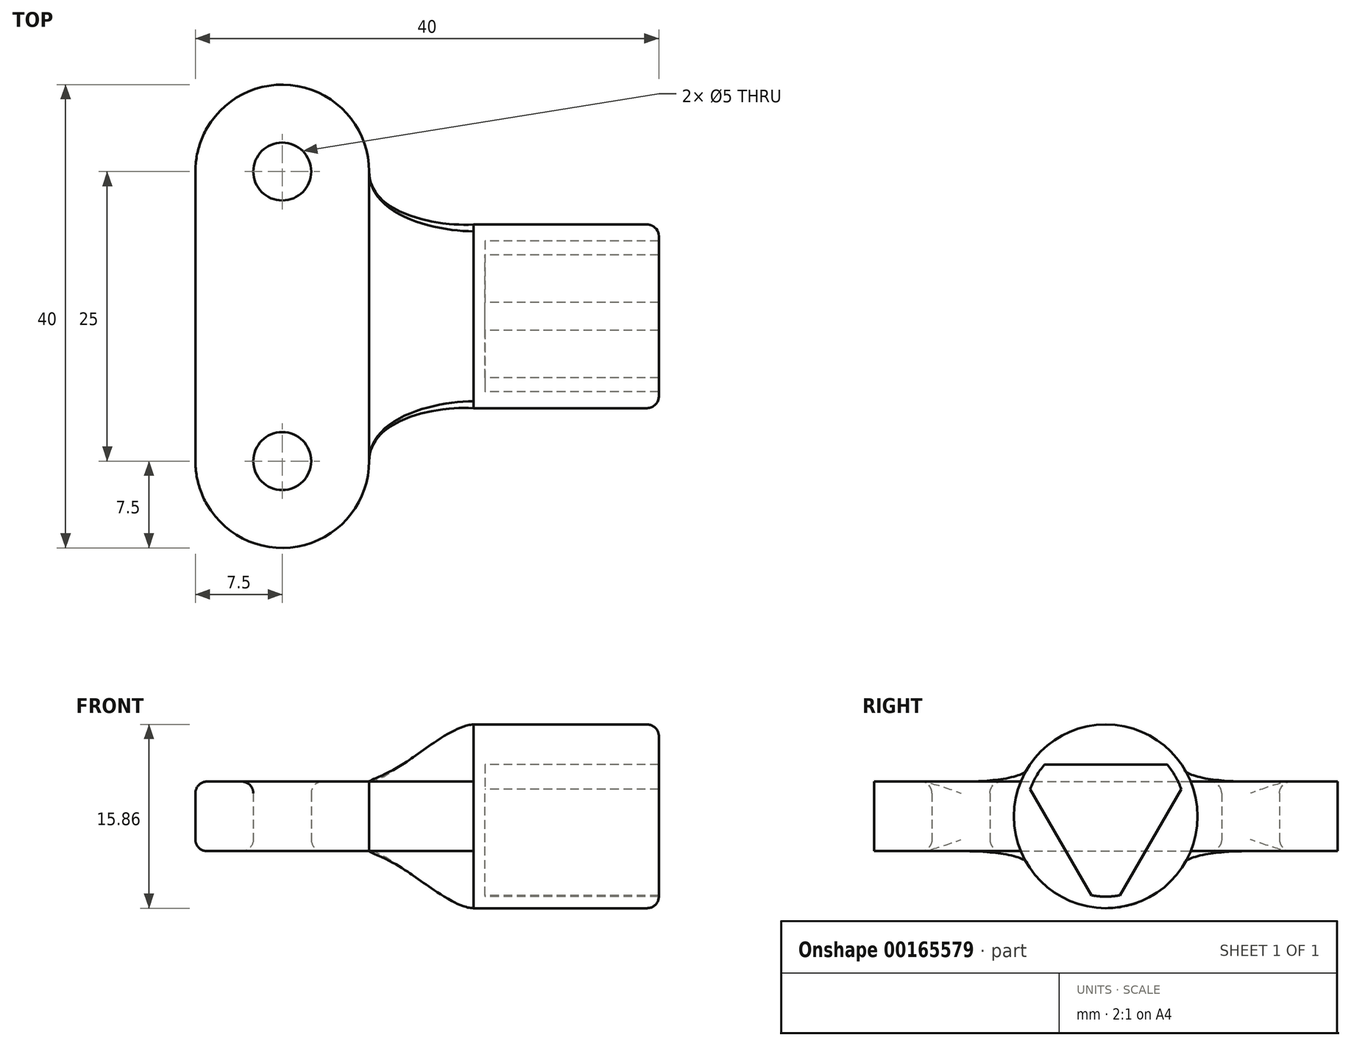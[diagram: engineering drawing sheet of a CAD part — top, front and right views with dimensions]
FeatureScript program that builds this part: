
annotation { "Feature Type Name" : "Feature", "Feature Type Description" : "" }
export const myFeature = defineFeature(function(context is Context, id is Id, definition is map)
    precondition{}
    {
        {
            var Q0;
            Q0=qCreatedBy(makeId("Right.planeOp"),FACE);
            cPlane(context, id + "F0", {"entities" : qUnion([Q0]), "cplaneType" : CPlaneType.OFFSET, "offset" : 0 * mm, "width" : 152.4 * mm, "height" : 152.4 * mm});
        }
        {
            var Q0;
            Q0=qCreatedBy(id+"F0.planeOp",FACE);
            var sketch = newSketch(context, id + "F1", { "sketchPlane" : qUnion([Q0])});
            skCircle(sketch, "E0", {"center": v(0, 0) * mm, "radius": 7.93 * mm});
            skCircle(sketch, "E1", {"center": v(0, 0) * mm, "radius": 6.93 * mm});
            skLineSegment(sketch, "E2", {"start": v(-5.3, 4.46) * mm, "end": v(5.3, 4.46) * mm});
            skLineSegment(sketch, "E3.1.0", {"start": v(-1.22, -6.82) * mm, "end": v(-6.52, 2.36) * mm});
            skLineSegment(sketch, "E3.2.0", {"start": v(6.52, 2.36) * mm, "end": v(1.22, -6.82) * mm});
            skCircle(sketch, "E4.cCircle", {"center": v(0, 0) * mm, "radius": 6.93 * mm, "construction": true});
            skLineSegment(sketch, "E4.0", {"start": v(0, -6.93) * mm, "end": v(-6, 3.46) * mm});
            skLineSegment(sketch, "E4.1", {"start": v(-6, 3.46) * mm, "end": v(6, 3.46) * mm});
            skLineSegment(sketch, "E4.2", {"start": v(6, 3.46) * mm, "end": v(0, -6.93) * mm});
            skLineSegment(sketch, "E5.bottom", {"start": v(-20, -7.93) * mm, "end": v(20, -7.93) * mm});
            skLineSegment(sketch, "E5.top", {"start": v(-20, 7.93) * mm, "end": v(20, 7.93) * mm});
            skLineSegment(sketch, "E5.left", {"start": v(-20, -7.93) * mm, "end": v(-20, 7.93) * mm});
            skLineSegment(sketch, "E5.right", {"start": v(20, -7.93) * mm, "end": v(20, 7.93) * mm});
            skSolve(sketch);
        }
        {
            var Q0;
            Q0=makeQuery(id+"F1.imprint","IMPRINT",FACE,{"disambiguationData":[TD([[makeQuery(id+"F1.imprint","IMPRINT",EDGE,{"derivedFrom":sQuery(id+"F1.wireOp",EDGE,"E0")}),1.0]])]});
            var Q1;
            {var subQ0=sQuery(id+"F1.wireOp",EDGE,"E2");Q1=makeQuery(id+"F1.imprint","IMPRINT",FACE,{"disambiguationData":[TD([[makeQuery(id+"F1.imprint","IMPRINT",EDGE,{"derivedFrom":subQ0}),1.0]])]});}
            var Q2;
            {var subQ0=sQuery(id+"F1.wireOp",EDGE,"E3.1.0");Q2=makeQuery(id+"F1.imprint","IMPRINT",FACE,{"disambiguationData":[TD([[makeQuery(id+"F1.imprint","IMPRINT",EDGE,{"derivedFrom":subQ0}),1.0]])]});}
            var Q3;
            {var subQ0=sQuery(id+"F1.wireOp",EDGE,"E3.2.0");Q3=makeQuery(id+"F1.imprint","IMPRINT",FACE,{"disambiguationData":[TD([[makeQuery(id+"F1.imprint","IMPRINT",EDGE,{"derivedFrom":subQ0}),1.0]])]});}
            var Q4;
            Q4=sQuery(id+"F1.wireOp",EDGE,"E0");
            var Q5;
            Q5=sQuery(id+"F1.wireOp",EDGE,"E1");
            var Q6;
            Q6=sQuery(id+"F1.wireOp",EDGE,"E2");
            var Q7;
            Q7=sQuery(id+"F1.wireOp",EDGE,"E3.1.0");
            var Q8;
            Q8=sQuery(id+"F1.wireOp",EDGE,"E3.2.0");
            extrude(context, id + "F2", {"entities" : qUnion([Q0, Q1, Q2, Q3]), "surfaceEntities" : qUnion([Q4, Q5, Q6, Q7, Q8]), "depth" : 15 * mm});
        }
        {
            var Q0;
            Q0=qCreatedBy(makeId("Top.planeOp"),FACE);
            var sketch = newSketch(context, id + "F3", { "sketchPlane" : qUnion([Q0])});
            skLineSegment(sketch, "E6", {"start": v(0, 0) * mm, "end": v(-7.34, 0) * mm, "construction": true});
            skLineSegment(sketch, "E7", {"start": v(-5, -7.93) * mm, "end": v(-5, -7.93) * mm});
            skLineSegment(sketch, "E8.trimOffspring", {"start": v(-12.53, 0) * mm, "end": v(-38.9, 0) * mm, "construction": true});
            skPoint(sketch, "E9.0.start.orphan", {"position": v(0, 7.93) * mm});
            skCircle(sketch, "E10", {"center": v(-17.5, -12.5) * mm, "radius": 2.5 * mm});
            skArc(sketch, "E11", {"start": v(-25, -12.5) * mm, "mid": v(-17.5, -20) * mm, "end": v(-10, -12.5) * mm});
            skLineSegment(sketch, "E12", {"start": v(-25, -12.5) * mm, "end": v(-25, 0) * mm});
            skLineSegment(sketch, "E13", {"start": v(-10, -12.5) * mm, "end": v(-10, 0) * mm});
            skLineSegment(sketch, "E14.MirrorCS", {"start": v(-10, 12.5) * mm, "end": v(-10, 0) * mm});
            skArc(sketch, "E15.MirrorCS", {"start": v(-25, 12.5) * mm, "mid": v(-17.5, 20) * mm, "end": v(-10, 12.5) * mm});
            skLineSegment(sketch, "E16.MirrorCS", {"start": v(-25, 12.5) * mm, "end": v(-25, 0) * mm});
            skCircle(sketch, "E17.MirrorC", {"center": v(-17.5, 12.5) * mm, "radius": 2.5 * mm});
            skSolve(sketch);
        }
        {
            var Q0;
            Q0=makeQuery(id+"F3.imprint","IMPRINT",FACE,{"disambiguationData":[TD([[makeQuery(id+"F3.imprint","IMPRINT",EDGE,{"derivedFrom":sQuery(id+"F3.wireOp",EDGE,"E10")}),-1.0]])]});
            extrude(context, id + "F4", {"entities" : qUnion([Q0]), "endBound" : BoundingType.SYMMETRIC, "depth" : 6 * mm});
        }
        {
            var Q0;
            Q0=qCreatedBy(makeId("Right.planeOp"),FACE);
            var sketch = newSketch(context, id + "F5", { "sketchPlane" : qUnion([Q0])});
            skArc(sketch, "E18.0", {"start": v(-7.93, 0) * mm, "mid": v(0, -7.93) * mm, "end": v(7.93, 0) * mm});
            skArc(sketch, "E19.0", {"start": v(7.93, 0) * mm, "mid": v(0, 7.93) * mm, "end": v(-7.93, 0) * mm});
            skLineSegment(sketch, "E20.bottom", {"start": v(-35.1, -7.93) * mm, "end": v(32.55, -7.93) * mm});
            skLineSegment(sketch, "E20.top", {"start": v(-35.1, 7.93) * mm, "end": v(32.55, 7.93) * mm});
            skLineSegment(sketch, "E20.left", {"start": v(-35.1, -7.93) * mm, "end": v(-35.1, 7.93) * mm});
            skLineSegment(sketch, "E20.right", {"start": v(32.55, -7.93) * mm, "end": v(32.55, 7.93) * mm});
            skSolve(sketch);
        }
        {
            var Q0;
            Q0=makeQuery(id+"F2.opExtrude","CAP_FACE",FACE,{"disambiguationData":[OSD([sQuery(id+"F1.wireOp",EDGE,"E0"),sQuery(id+"F1.wireOp",EDGE,"E1"),sQuery(id+"F1.wireOp",EDGE,"E2"),sQuery(id+"F1.wireOp",EDGE,"E3.1.0"),sQuery(id+"F1.wireOp",EDGE,"E3.2.0")])],"isStart":true});
            var sketch = newSketch(context, id + "F6", { "sketchPlane" : qUnion([Q0])});
            skCircle(sketch, "E21.0", {"center": v(0, 0) * mm, "radius": 7.93 * mm});
            skSolve(sketch);
        }
        {
            var Q0;
            {var subQ5=sQuery(id+"F1.wireOp",EDGE,"E2");Q0=makeQuery(id+"F6.imprint","IMPRINT",FACE,{"disambiguationData":[TD([[makeQuery(id+"F6.imprint","IMPRINT",EDGE,{"derivedFrom":makeQuery(id+"F2.opExtrude","CAP_EDGE",EDGE,{"disambiguationData":[OSD([subQ5])],"isStart":true})}),1.0]])]});}
            var Q1;
            Q1=makeQuery(id+"F6.imprint","IMPRINT",FACE,{"disambiguationData":[TD([[makeQuery(id+"F6.imprint","IMPRINT",EDGE,{"derivedFrom":sQuery(id+"F6.wireOp",EDGE,"E21.0")}),-1.0]])]});
            extrude(context, id + "F7", {"entities" : qUnion([Q0, Q1]), "operationType" : NewBodyOperationType.ADD, "depth" : 1 * mm});
        }
        {
            var Q0;
            Q0=makeQuery(id+"F4.opExtrude","CAP_FACE",FACE,{"disambiguationData":[OSD([sQuery(id+"F3.wireOp",EDGE,"E10"),sQuery(id+"F3.wireOp",EDGE,"E11"),sQuery(id+"F3.wireOp",EDGE,"E12"),sQuery(id+"F3.wireOp",EDGE,"E13"),sQuery(id+"F3.wireOp",EDGE,"E14.MirrorCS"),sQuery(id+"F3.wireOp",EDGE,"E15.MirrorCS"),sQuery(id+"F3.wireOp",EDGE,"E16.MirrorCS"),sQuery(id+"F3.wireOp",EDGE,"E17.MirrorC")])],"isStart":false});
            var sketch = newSketch(context, id + "F8", { "sketchPlane" : qUnion([Q0])});
            skFitSpline(sketch, "E22", {"points": [v(-1, -7.34) * mm, v(-10, -12.5) * mm], "startDerivative": vector(-9.67, 0) * mm, "endDerivative": vector(0, -11.48) * mm});
            skFitSpline(sketch, "E23.MirrorCS", {"points": [v(-1, 7.34) * mm, v(-10, 12.5) * mm], "startDerivative": vector(-9.67, 0) * mm, "endDerivative": vector(0, 11.48) * mm});
            skSolve(sketch);
        }
        {
            var Q0;
            Q0=makeQuery(id+"F4.opExtrude","CAP_FACE",FACE,{"disambiguationData":[OSD([sQuery(id+"F3.wireOp",EDGE,"E10"),sQuery(id+"F3.wireOp",EDGE,"E11"),sQuery(id+"F3.wireOp",EDGE,"E12"),sQuery(id+"F3.wireOp",EDGE,"E13"),sQuery(id+"F3.wireOp",EDGE,"E14.MirrorCS"),sQuery(id+"F3.wireOp",EDGE,"E15.MirrorCS"),sQuery(id+"F3.wireOp",EDGE,"E16.MirrorCS"),sQuery(id+"F3.wireOp",EDGE,"E17.MirrorC")])],"isStart":true});
            var sketch = newSketch(context, id + "F9", { "sketchPlane" : qUnion([Q0])});
            skFitSpline(sketch, "E24", {"points": [v(-1, -7.34) * mm, v(-10, -12.5) * mm], "startDerivative": vector(-9.67, 0) * mm, "endDerivative": vector(0, -11.48) * mm});
            skFitSpline(sketch, "E25.MirrorCS", {"points": [v(-1, 7.34) * mm, v(-10, 12.5) * mm], "startDerivative": vector(-9.67, 0) * mm, "endDerivative": vector(0, 11.48) * mm});
            skSolve(sketch);
        }
        {
            var Q0;
            Q0=qCreatedBy(makeId("Front.planeOp"),FACE);
            var sketch = newSketch(context, id + "F10", { "sketchPlane" : qUnion([Q0])});
            skFitSpline(sketch, "E26", {"points": [v(-1, 7.93) * mm, v(-10, 3) * mm], "startDerivative": vector(-6.94, 0) * mm, "endDerivative": vector(-5.27, 0) * mm});
            skLineSegment(sketch, "E27", {"start": v(-1, 7.93) * mm, "end": v(15, 7.93) * mm});
            skFitSpline(sketch, "E28.MirrorCS", {"points": [v(-1, -7.93) * mm, v(-10, -3) * mm], "startDerivative": vector(-6.94, 0) * mm, "endDerivative": vector(-5.27, 0) * mm});
            skSolve(sketch);
        }
        {
            var Q2;
            Q2=makeQuery(id+"F4.opExtrude","SWEPT_FACE",FACE,{"disambiguationData":[OSD([sQuery(id+"F3.wireOp",EDGE,"E13"),sQuery(id+"F3.wireOp",EDGE,"E14.MirrorCS")])]});
            var Q3;
            Q3=makeQuery(id+"F7.opExtrude","CAP_FACE",FACE,{"disambiguationData":[OSD([sQuery(id+"F6.wireOp",EDGE,"E21.0")])],"isStart":false});
            var Q4;
            Q4=sQuery(id+"F9.wireOp",EDGE,"E25.MirrorCS");
            var Q5;
            Q5=sQuery(id+"F8.wireOp",EDGE,"E22");
            var Q6;
            Q6=sQuery(id+"F8.wireOp",EDGE,"E23.MirrorCS");
            var Q7;
            Q7=sQuery(id+"F9.wireOp",EDGE,"E24");
            var Q8;
            Q8=sQuery(id+"F10.wireOp",EDGE,"E26");
            var Q9;
            Q9=sQuery(id+"F10.wireOp",EDGE,"E28.MirrorCS");
            loft(context, id + "F11", {"operationType" : NewBodyOperationType.ADD, "addGuides" : true, "sheetProfilesArray" : [{ "sheetProfileEntities" : qUnion([Q2]) }, { "sheetProfileEntities" : qUnion([Q3]) }], "guidesArray" : [{ "guideEntities" : qUnion([Q4]), "guideDerivativeType" : LoftGuideDerivativeType.DEFAULT, "guideDerivativeMagnitude" : 1 }, { "guideEntities" : qUnion([Q5]), "guideDerivativeType" : LoftGuideDerivativeType.DEFAULT, "guideDerivativeMagnitude" : 1 }, { "guideEntities" : qUnion([Q6]), "guideDerivativeType" : LoftGuideDerivativeType.DEFAULT, "guideDerivativeMagnitude" : 1 }, { "guideEntities" : qUnion([Q7]), "guideDerivativeType" : LoftGuideDerivativeType.DEFAULT, "guideDerivativeMagnitude" : 1 }, { "guideEntities" : qUnion([Q8]), "guideDerivativeType" : LoftGuideDerivativeType.DEFAULT, "guideDerivativeMagnitude" : 1 }, { "guideEntities" : qUnion([Q9]), "guideDerivativeType" : LoftGuideDerivativeType.DEFAULT, "guideDerivativeMagnitude" : 1 }]});
        }
        {
            var Q0;
            Q0=makeQuery(id+"F4.opExtrude","CAP_EDGE",EDGE,{"disambiguationData":[OSD([sQuery(id+"F3.wireOp",EDGE,"E12"),sQuery(id+"F3.wireOp",EDGE,"E16.MirrorCS")])],"isStart":false});
            var Q1;
            Q1=makeQuery(id+"F4.opExtrude","CAP_EDGE",EDGE,{"disambiguationData":[OSD([sQuery(id+"F3.wireOp",EDGE,"E12"),sQuery(id+"F3.wireOp",EDGE,"E16.MirrorCS")])],"isStart":true});
            var Q2;
            Q2=makeQuery(id+"F4.opExtrude","CAP_EDGE",EDGE,{"disambiguationData":[OSD([sQuery(id+"F3.wireOp",EDGE,"E17.MirrorC")])],"isStart":false});
            var Q3;
            Q3=makeQuery(id+"F4.opExtrude","CAP_EDGE",EDGE,{"disambiguationData":[OSD([sQuery(id+"F3.wireOp",EDGE,"E10")])],"isStart":false});
            var Q4;
            Q4=makeQuery(id+"F4.opExtrude","CAP_EDGE",EDGE,{"disambiguationData":[OSD([sQuery(id+"F3.wireOp",EDGE,"E10")])],"isStart":true});
            var Q5;
            Q5=makeQuery(id+"F4.opExtrude","CAP_EDGE",EDGE,{"disambiguationData":[OSD([sQuery(id+"F3.wireOp",EDGE,"E17.MirrorC")])],"isStart":true});
            fillet(context, id + "F12", {"entities" : qUnion([Q0, Q1, Q2, Q3, Q4, Q5]), "radius" : 1 * mm, "allowEdgeOverflow" : false});
        }
        {
            var Q0;
            Q0=makeQuery(id+"F2.opExtrude","CAP_EDGE",EDGE,{"disambiguationData":[OSD([sQuery(id+"F1.wireOp",EDGE,"E0")])],"isStart":false});
            fillet(context, id + "F13", {"entities" : qUnion([Q0]), "radius" : 1 * mm, "tangentPropagation" : true, "allowEdgeOverflow" : false});
        }
    });
